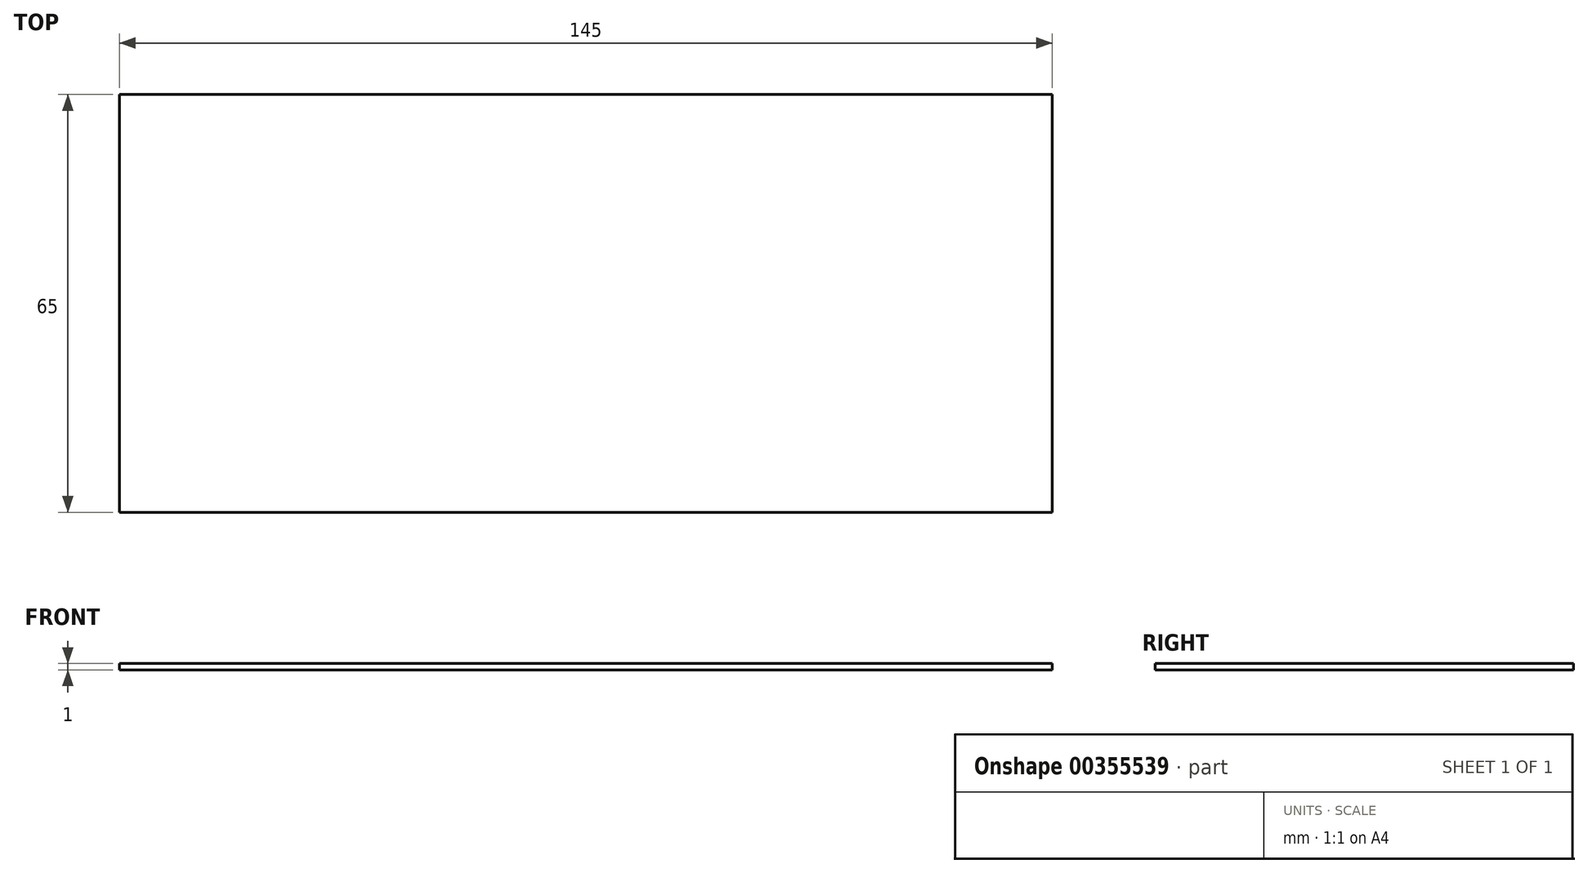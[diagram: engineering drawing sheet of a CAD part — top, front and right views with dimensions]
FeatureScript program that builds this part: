
annotation { "Feature Type Name" : "Feature", "Feature Type Description" : "" }
export const myFeature = defineFeature(function(context is Context, id is Id, definition is map)
    precondition{}
    {
        {
            var Q0;
            Q0=qCreatedBy(makeId("Top.planeOp"),FACE);
            var sketch = newSketch(context, id + "F0", { "sketchPlane" : qUnion([Q0])});
            skLineSegment(sketch, "E0.bottom", {"start": v(0, 0) * mm, "end": v(145, 0) * mm});
            skLineSegment(sketch, "E0.top", {"start": v(0, 65) * mm, "end": v(145, 65) * mm});
            skLineSegment(sketch, "E0.left", {"start": v(0, 0) * mm, "end": v(0, 65) * mm});
            skLineSegment(sketch, "E0.right", {"start": v(145, 0) * mm, "end": v(145, 65) * mm});
            skSolve(sketch);
        }
        {
            var Q0;
            Q0=makeQuery(id+"F0.imprint","IMPRINT",FACE,{"disambiguationData":[TD([[makeQuery(id+"F0.imprint","IMPRINT",EDGE,{"derivedFrom":sQuery(id+"F0.wireOp",EDGE,"E0.bottom")}),1.0]])]});
            extrude(context, id + "F1", {"entities" : qUnion([Q0]), "depth" : 1 * mm});
        }
    });
